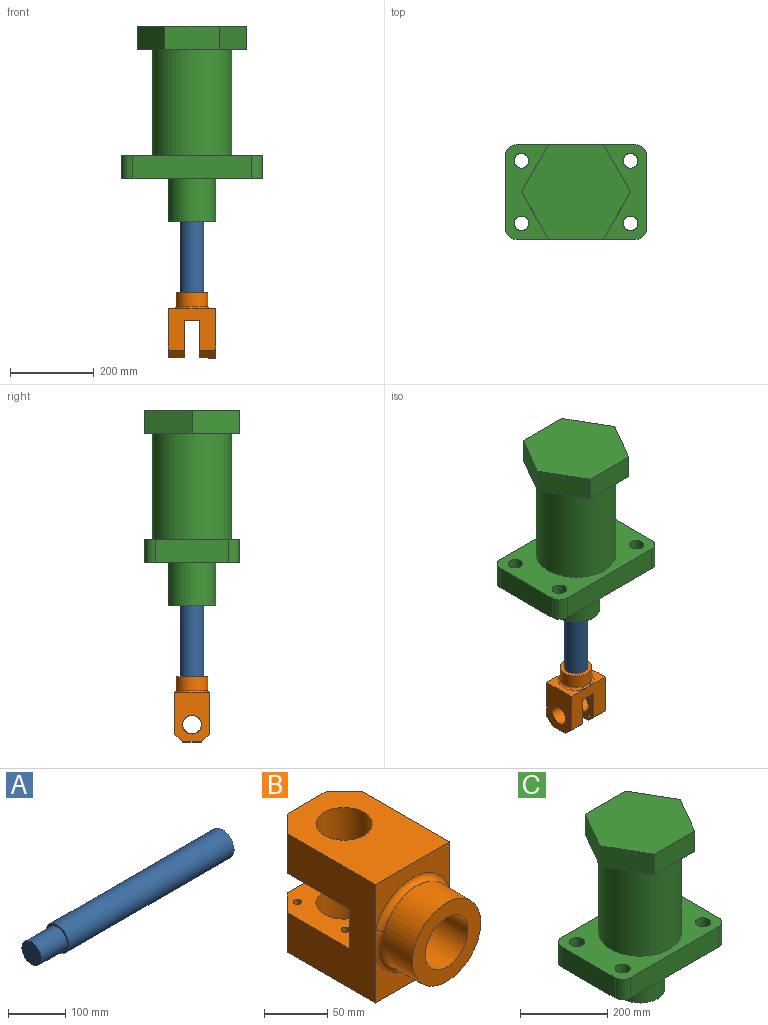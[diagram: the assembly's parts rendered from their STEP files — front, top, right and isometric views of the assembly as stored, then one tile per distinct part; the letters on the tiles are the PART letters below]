
ASSEMBLY  parts=3 mates=2
PART A: 5 faces, bbox 469.9x57.2x57.2 mm
  f0: cylinder r=28.57mm len=406.4mm, axis (-1,0,0), area 72965.9mm2, adj f1,f2
  f1: plane 57.15x57.15mm, normal (1,0,0), area 2565.2mm2, adj f0
  f2: plane 57.15x57.15mm, normal (-1,0,0), area 783.8mm2, adj f0,f3
  f3: cylinder r=23.81mm len=63.5mm, axis (1,0,0), area 9500.8mm2, adj f2,f4
  f4: plane 47.63x47.63mm, normal (-1,0,0), area 1781.4mm2, adj f3
PART B: 27 faces, bbox 89.5x155.7x114.5 mm
  f0: plane 82.55x44.47mm, normal (0,-1,0), area 1821.3mm2, adj f6,f9,f10,f24
  f1: plane 82.55x38.1mm, normal (0,1,0), area 2066.6mm2, adj f2,f8,f9,f10,f20
  f2: plane 88.9x82.55mm, normal (0,0,-1), area 5420.5mm2, adj f1,f3,f9,f10,f13,f14,f16
  f3: plane 44.45x38.1mm, normal (0,1,0), area 1693.5mm2, adj f2,f4,f13,f14
  f4: plane 117.48x82.55mm, normal (0,0,1), area 7779.3mm2, adj f3,f5,f9,f10,f13,f14,f16
  f5: plane 82.55x44.47mm, normal (0,-1,0), area 1821.3mm2, adj f4,f9,f10,f25
  f6: plane 117.48x82.55mm, normal (0,0,-1), area 7712.4mm2, adj f0,f7,f9,f10,f11,f12,f15,f17
  f7: plane 44.45x38.1mm, normal (0,1,0), area 1693.5mm2, adj f6,f8,f11,f12
  f8: plane 88.9x82.55mm, normal (0,0,1), area 5353.5mm2, adj f1,f7,f9,f10,f11,f12,f15,f17
  f9: plane 114.46x98.59mm, normal (1,0,0), area 8588.7mm2, adj f0,f1,f2,f4,f5,f6,f8,f11
  f10: plane 114.46x98.59mm, normal (-1,0,0), area 8588.7mm2, adj f0,f1,f2,f4,f5,f6,f8,f12
  f11: plane 38.1x19.05mm, normal (0.71,0.71,0), area 1026.4mm2, adj f6,f7,f8,f9
  f12: plane 38.1x19.05mm, normal (-0.71,0.71,0), area 1026.4mm2, adj f6,f7,f8,f10
  f13: plane 38.1x19.05mm, normal (-0.71,0.71,0), area 1026.4mm2, adj f2,f3,f4,f10
  f14: plane 38.1x19.05mm, normal (0.71,0.71,0), area 1026.4mm2, adj f2,f3,f4,f9
  f15: cylinder r=22.25mm len=44.5mm, axis (0,0,-1), area 5326.5mm2, adj f6,f8
  f16: cylinder r=22.25mm len=44.5mm, axis (0,0,-1), area 5326.5mm2, adj f2,f4
  f17: cylinder r=3.26mm len=38.1mm, axis (0,0,-1), area 781.3mm2, adj f6,f8
  f18: cylinder r=3.26mm len=38.1mm, axis (0,0,-1), area 781.3mm2, adj f6,f8
  f19: cylinder r=23.81mm len=63.5mm, axis (0,-1,0), area 9500.8mm2, adj f20,f22
  f20: cone r=0mm half-angle=59deg, axis (0,-1,0), area 820mm2, adj f1,f19
  f21: cylinder r=38.1mm len=76.2mm, axis (0,1,0), area 7904.6mm2, adj f22,f23,f24,f25,f26
  f22: plane 76.2x76.2mm, normal (0,-1,0), area 2779mm2, adj f19,f21
  f23: bspline ~28.49x5.72mm, area 157.2mm2, adj f10,f21,f24,f25
  f24: torus R=43.18mm, axis (0,1,0), area 811.3mm2, adj f0,f21,f23,f26
  f25: torus R=43.18mm, axis (0,1,0), area 811.3mm2, adj f5,f21,f23,f26
  f26: bspline ~28.49x5.72mm, area 157.2mm2, adj f9,f21,f24,f25
PART C: 27 faces, bbox 336.6x225.6x466.7 mm
  f0: cylinder r=25.4mm len=57.15mm, axis (0,0,-1), area 2280.2mm2, adj f1,f7,f8,f9
  f1: plane 285.75x57.15mm, normal (0,-1,0), area 16330.6mm2, adj f0,f2,f8,f9
  f2: cylinder r=25.4mm len=57.15mm, axis (0,0,-1), area 2280.2mm2, adj f1,f3,f8,f9
  f3: plane 174.63x57.15mm, normal (1,0,0), area 9979.8mm2, adj f2,f4,f8,f9
  f4: cylinder r=25.4mm len=57.15mm, axis (0,0,-1), area 2280.2mm2, adj f3,f5,f8,f9
  f5: plane 285.75x57.15mm, normal (0,1,0), area 16330.6mm2, adj f4,f6,f8,f9
  f6: cylinder r=25.4mm len=57.15mm, axis (0,0,-1), area 2280.2mm2, adj f5,f7,f8,f9
  f7: plane 174.63x57.15mm, normal (-1,0,0), area 9979.8mm2, adj f0,f6,f8,f9
  f8: plane 336.55x225.43mm, normal (0,0,1), area 42978.7mm2, adj f0,f1,f2,f3,f4,f5,f6,f7
  f9: plane 336.55x225.43mm, normal (0,0,-1), area 61220.2mm2, adj f0,f1,f2,f3,f4,f5,f6,f7
  f10: cylinder r=95.25mm len=250.83mm, axis (0,0,-1), area 150112.1mm2, adj f8,f18
  f11: plane 112.78x65.11mm, normal (-0.87,0.5,0), area 7442.5mm2, adj f12,f16,f17,f18
  f12: plane 112.78x65.11mm, normal (-0.87,-0.5,0), area 7442.5mm2, adj f11,f13,f17,f18
  f13: plane 130.23x57.15mm, normal (0,-1,0), area 7442.5mm2, adj f12,f14,f17,f18
  f14: plane 112.78x65.11mm, normal (0.87,-0.5,0), area 7442.5mm2, adj f13,f15,f17,f18
  f15: plane 112.78x65.11mm, normal (0.87,0.5,0), area 7442.5mm2, adj f14,f16,f17,f18
  f16: plane 130.23x57.15mm, normal (0,1,0), area 7442.5mm2, adj f11,f15,f17,f18
  f17: plane 260.46x225.56mm, normal (0,0,1), area 44061.6mm2, adj f11,f12,f13,f14,f15,f16
  f18: plane 260.46x225.56mm, normal (0,0,-1), area 15559.4mm2, adj f10,f11,f12,f13,f14,f15,f16
  f19: cylinder r=17.46mm len=57.15mm, axis (0,0,-1), area 6270.5mm2, adj f8,f9
  f20: cylinder r=17.46mm len=57.15mm, axis (0,0,-1), area 6270.5mm2, adj f8,f9
  f21: cylinder r=17.46mm len=57.15mm, axis (0,0,-1), area 6270.5mm2, adj f8,f9
  f22: cylinder r=17.46mm len=57.15mm, axis (0,0,-1), area 6270.5mm2, adj f8,f9
  f23: cylinder r=57.15mm len=114.3mm, axis (0,0,1), area 36482.9mm2, adj f9,f24
  f24: plane 114.3x114.3mm, normal (0,0,-1), area 7695.6mm2, adj f23,f25
  f25: cylinder r=28.57mm len=406.4mm, axis (0,0,-1), area 72965.9mm2, adj f24,f26
  f26: cone r=0mm half-angle=59deg, axis (0,0,-1), area 2992.7mm2, adj f25
PLACE A rot(axis=(0,-1,0),90deg) t=(7.97,91.58,-273.07)mm
PLACE B rot(axis=(-0.58,-0.58,0.58),120deg) t=(7.97,91.58,-350.86)mm
PLACE C t=(7.97,91.58,-1.29)mm
MATE slider A.f0 <-> C.f10  axis (0,0,-1) through (7.97,91.58,133.33)mm
MATE fastened B.f24 <-> A.f0  axis (0,0,1) through (7.97,91.58,-273.07)mm
